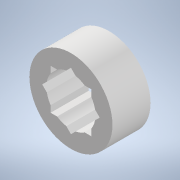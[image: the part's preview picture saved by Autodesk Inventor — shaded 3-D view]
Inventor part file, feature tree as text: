
AUTODESK INVENTOR PART (.ipt)
format: ipt  version: 2022.3 (Build 263350000, 350)  size: 129,024 bytes
history: native  units: mm
features: other x3, reference x2, sketch x1, plane x1, extrude x1
ambient origin geometry x8: Origin, YZ Plane, XZ Plane, XY Plane, X Axis, Y Axis, Z Axis, Center Point
bodies: Solid1 (feature_tree)
feature tree (8):
  sketch  "Sketch1"  dims[d0=1.2mm d1=10.0mm d2=0.0mm]
  plane  "Work Plane1"
  extrude  "Extrusion1"  Depth=10.0mm TaperAngle=0.0deg
  reference  "Reference1"
  reference  "Reference2"
  other  "Assembly3"
  other  "kolo:1"
  other  "bok:1"
